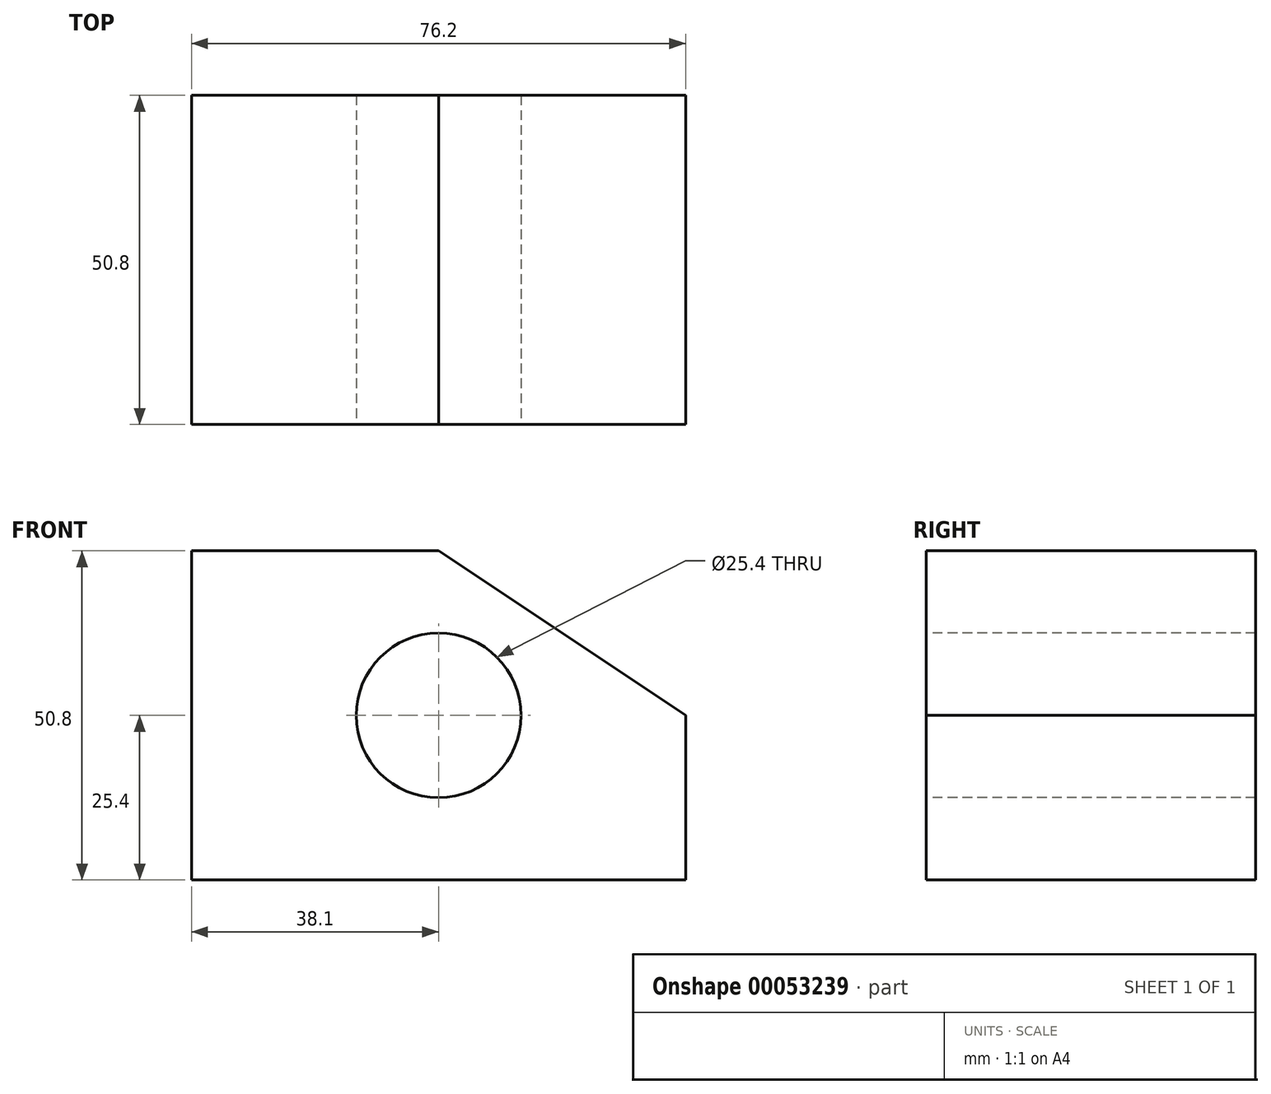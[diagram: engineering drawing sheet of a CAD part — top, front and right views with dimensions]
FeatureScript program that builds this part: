
annotation { "Feature Type Name" : "Feature", "Feature Type Description" : "" }
export const myFeature = defineFeature(function(context is Context, id is Id, definition is map)
    precondition{}
    {
        {
            var Q0;
            Q0=qCreatedBy(makeId("Front.planeOp"),FACE);
            var sketch = newSketch(context, id + "F0", { "sketchPlane" : qUnion([Q0])});
            skLineSegment(sketch, "E0", {"start": v(0, 0) * mm, "end": v(0, 50.8) * mm});
            skLineSegment(sketch, "E1", {"start": v(0, 50.8) * mm, "end": v(38.1, 50.8) * mm});
            skLineSegment(sketch, "E2", {"start": v(38.1, 50.8) * mm, "end": v(76.2, 25.4) * mm});
            skLineSegment(sketch, "E3", {"start": v(76.2, 25.4) * mm, "end": v(76.2, 0) * mm});
            skLineSegment(sketch, "E4", {"start": v(76.2, 0) * mm, "end": v(0, 0) * mm});
            skSolve(sketch);
        }
        {
            var Q0;
            Q0 = qSketchRegion(id + "F0", true);
            extrude(context, id + "F1", {"entities" : qUnion([Q0]), "depth" : 50.8 * mm});
        }
        {
            var Q0;
            Q0=makeQuery(id+"F1.opExtrude","CAP_FACE",FACE,{"disambiguationData":[OSD([sQuery(id+"F0.wireOp",EDGE,"E0"),sQuery(id+"F0.wireOp",EDGE,"E1"),sQuery(id+"F0.wireOp",EDGE,"E2"),sQuery(id+"F0.wireOp",EDGE,"E3"),sQuery(id+"F0.wireOp",EDGE,"E4")])],"isStart":false});
            var sketch = newSketch(context, id + "F2", { "sketchPlane" : qUnion([Q0])});
            skCircle(sketch, "E5", {"center": v(38.1, 25.4) * mm, "radius": 12.7 * mm});
            skSolve(sketch);
        }
        {
            var Q0;
            Q0 = qSketchRegion(id + "F2", true);
            extrude(context, id + "F3", {"entities" : qUnion([Q0]), "operationType" : NewBodyOperationType.REMOVE, "oppositeDirection" : true, "depth" : 50.8 * mm});
        }
    });
